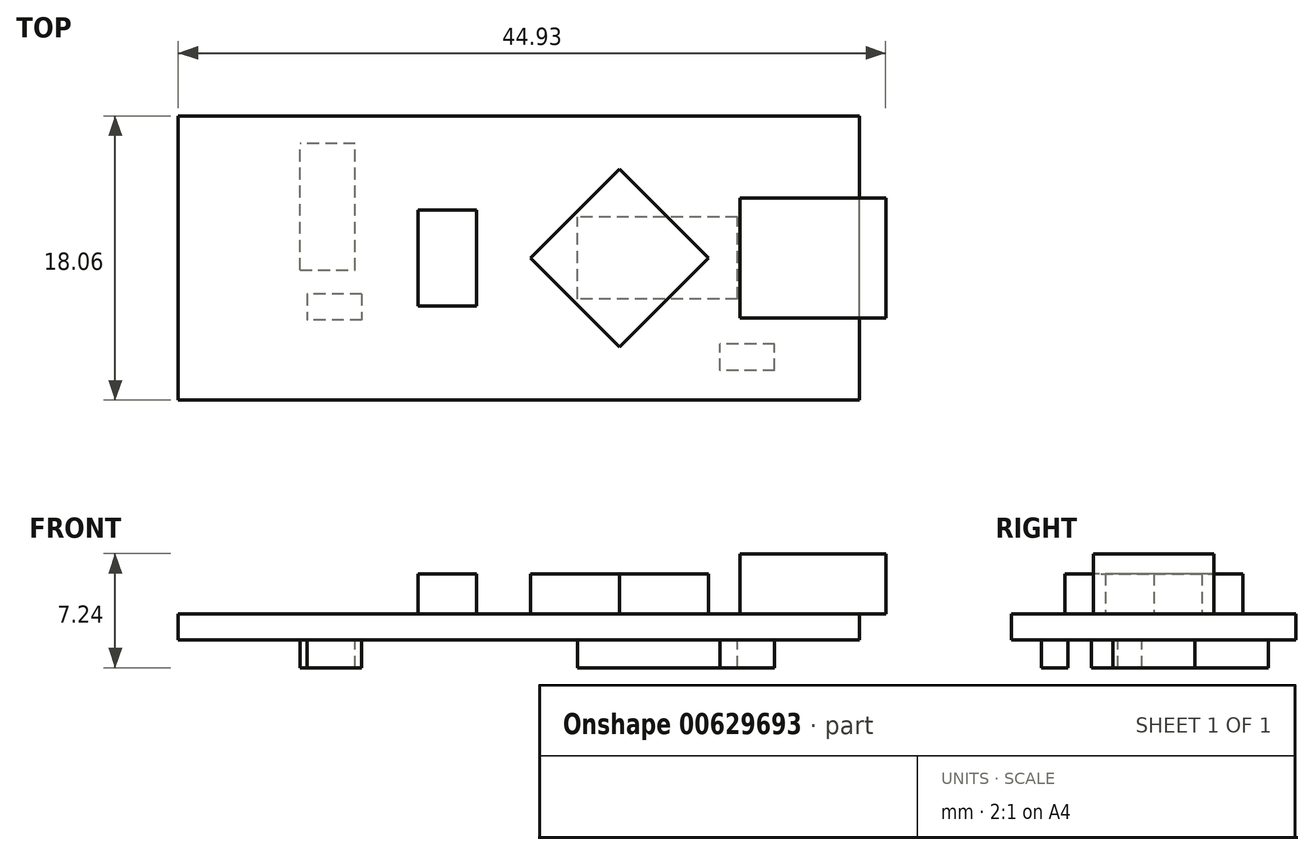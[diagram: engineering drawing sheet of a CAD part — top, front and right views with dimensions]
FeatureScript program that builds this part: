
annotation { "Feature Type Name" : "Feature", "Feature Type Description" : "" }
export const myFeature = defineFeature(function(context is Context, id is Id, definition is map)
    precondition{}
    {
        {
            var Q0;
            Q0=qCreatedBy(makeId("Top.planeOp"),FACE);
            var sketch = newSketch(context, id + "F0", { "sketchPlane" : qUnion([Q0])});
            skLineSegment(sketch, "E0.bottom", {"start": v(21.63, -9.03) * mm, "end": v(-21.63, -9.03) * mm});
            skLineSegment(sketch, "E0.top", {"start": v(21.63, 9.03) * mm, "end": v(-21.63, 9.03) * mm});
            skLineSegment(sketch, "E0.left", {"start": v(21.63, -9.03) * mm, "end": v(21.63, 9.03) * mm});
            skLineSegment(sketch, "E0.right", {"start": v(-21.63, -9.03) * mm, "end": v(-21.63, 9.03) * mm});
            skPoint(sketch, "E0.middle", {"position": v(0, 0) * mm});
            skSolve(sketch);
        }
        {
            var Q0;
            Q0 = qSketchRegion(id + "F0", true);
            extrude(context, id + "F1", {"entities" : qUnion([Q0]), "endBound" : BoundingType.SYMMETRIC, "depth" : 1.65 * mm, "offsetDistance" : 25.4 * mm});
        }
        {
            var Q0;
            Q0=makeQuery(id+"F1.opExtrude","CAP_FACE",FACE,{"disambiguationData":[OSD([sQuery(id+"F0.wireOp",EDGE,"E0.bottom"),sQuery(id+"F0.wireOp",EDGE,"E0.top"),sQuery(id+"F0.wireOp",EDGE,"E0.left"),sQuery(id+"F0.wireOp",EDGE,"E0.right")])],"isStart":false});
            var sketch = newSketch(context, id + "F2", { "sketchPlane" : qUnion([Q0])});
            skLineSegment(sketch, "E1.bottom", {"start": v(14.03, 3.82) * mm, "end": v(23.3, 3.82) * mm});
            skLineSegment(sketch, "E1.top", {"start": v(14.03, -3.82) * mm, "end": v(23.3, -3.82) * mm});
            skLineSegment(sketch, "E1.left", {"start": v(14.03, 3.82) * mm, "end": v(14.03, -3.82) * mm});
            skLineSegment(sketch, "E1.right", {"start": v(23.3, 3.82) * mm, "end": v(23.3, -3.82) * mm});
            skPoint(sketch, "E1.middle", {"position": v(18.67, 0) * mm});
            skSolve(sketch);
        }
        {
            var Q0;
            Q0 = qSketchRegion(id + "F2", true);
            extrude(context, id + "F3", {"entities" : qUnion([Q0]), "operationType" : NewBodyOperationType.ADD, "depth" : 3.8 * mm, "offsetDistance" : 25.4 * mm});
        }
        {
            var Q0;
            Q0=makeQuery(id+"F1.opExtrude","CAP_FACE",FACE,{"disambiguationData":[OSD([sQuery(id+"F0.wireOp",EDGE,"E0.bottom"),sQuery(id+"F0.wireOp",EDGE,"E0.top"),sQuery(id+"F0.wireOp",EDGE,"E0.left"),sQuery(id+"F0.wireOp",EDGE,"E0.right")])],"isStart":false});
            var sketch = newSketch(context, id + "F4", { "sketchPlane" : qUnion([Q0])});
            skLineSegment(sketch, "E2.bottom", {"start": v(-2.68, 3.06) * mm, "end": v(-6.39, 3.06) * mm});
            skLineSegment(sketch, "E2.top", {"start": v(-2.68, -3.06) * mm, "end": v(-6.39, -3.06) * mm});
            skLineSegment(sketch, "E2.left", {"start": v(-2.68, 3.06) * mm, "end": v(-2.68, -3.06) * mm});
            skLineSegment(sketch, "E2.right", {"start": v(-6.39, 3.06) * mm, "end": v(-6.39, -3.06) * mm});
            skPoint(sketch, "E2.middle", {"position": v(-4.53, 0) * mm});
            skLineSegment(sketch, "E3", {"start": v(6.39, 5.66) * mm, "end": v(12.05, 0) * mm});
            skLineSegment(sketch, "E4", {"start": v(12.05, 0) * mm, "end": v(6.39, -5.66) * mm});
            skLineSegment(sketch, "E5", {"start": v(6.39, -5.66) * mm, "end": v(0.73, 0) * mm});
            skLineSegment(sketch, "E6", {"start": v(0.73, 0) * mm, "end": v(6.39, 5.66) * mm});
            skSolve(sketch);
        }
        {
            var Q0;
            Q0 = qSketchRegion(id + "F4", true);
            extrude(context, id + "F5", {"entities" : qUnion([Q0]), "operationType" : NewBodyOperationType.ADD, "depth" : 2.54 * mm, "offsetDistance" : 25.4 * mm});
        }
        {
            var Q0;
            Q0=makeQuery(id+"F1.opExtrude","CAP_FACE",FACE,{"disambiguationData":[OSD([sQuery(id+"F0.wireOp",EDGE,"E0.bottom"),sQuery(id+"F0.wireOp",EDGE,"E0.top"),sQuery(id+"F0.wireOp",EDGE,"E0.left"),sQuery(id+"F0.wireOp",EDGE,"E0.right")])],"isStart":true});
            var sketch = newSketch(context, id + "F6", { "sketchPlane" : qUnion([Q0])});
            skLineSegment(sketch, "E7.bottom", {"start": v(13.88, 2.6) * mm, "end": v(3.72, 2.6) * mm});
            skLineSegment(sketch, "E7.top", {"start": v(13.88, -2.6) * mm, "end": v(3.72, -2.6) * mm});
            skLineSegment(sketch, "E7.left", {"start": v(13.88, 2.6) * mm, "end": v(13.88, -2.6) * mm});
            skLineSegment(sketch, "E7.right", {"start": v(3.72, 2.6) * mm, "end": v(3.72, -2.6) * mm});
            skPoint(sketch, "E7.middle", {"position": v(8.8, 0) * mm});
            skLineSegment(sketch, "E8.bottom", {"start": v(16.25, 7.14) * mm, "end": v(12.77, 7.14) * mm});
            skLineSegment(sketch, "E8.top", {"start": v(16.25, 5.47) * mm, "end": v(12.77, 5.47) * mm});
            skLineSegment(sketch, "E8.left", {"start": v(16.25, 7.14) * mm, "end": v(16.25, 5.47) * mm});
            skLineSegment(sketch, "E8.right", {"start": v(12.77, 7.14) * mm, "end": v(12.77, 5.47) * mm});
            skPoint(sketch, "E8.middle", {"position": v(14.5, 6.3) * mm});
            skLineSegment(sketch, "E9.top", {"start": v(-10.39, -7.29) * mm, "end": v(-13.9, -7.29) * mm});
            skLineSegment(sketch, "E9.left", {"start": v(-10.39, 0.76) * mm, "end": v(-10.39, -7.29) * mm});
            skLineSegment(sketch, "E9.right", {"start": v(-13.9, 0.76) * mm, "end": v(-13.9, -7.29) * mm});
            skLineSegment(sketch, "E10.bottom", {"start": v(-9.97, 2.27) * mm, "end": v(-13.45, 2.27) * mm});
            skLineSegment(sketch, "E10.top", {"start": v(-9.97, 3.95) * mm, "end": v(-13.45, 3.95) * mm});
            skLineSegment(sketch, "E10.left", {"start": v(-9.97, 2.27) * mm, "end": v(-9.97, 3.95) * mm});
            skLineSegment(sketch, "E10.right", {"start": v(-13.45, 2.27) * mm, "end": v(-13.45, 3.95) * mm});
            skPoint(sketch, "E10.middle", {"position": v(-11.71, 3.11) * mm});
            skLineSegment(sketch, "E11", {"start": v(-13.9, 0.76) * mm, "end": v(-10.39, 0.76) * mm});
            skSolve(sketch);
        }
        {
            var Q0;
            Q0 = qSketchRegion(id + "F6", true);
            extrude(context, id + "F7", {"entities" : qUnion([Q0]), "operationType" : NewBodyOperationType.ADD, "depth" : 1.78 * mm, "offsetDistance" : 25.4 * mm});
        }
    });
